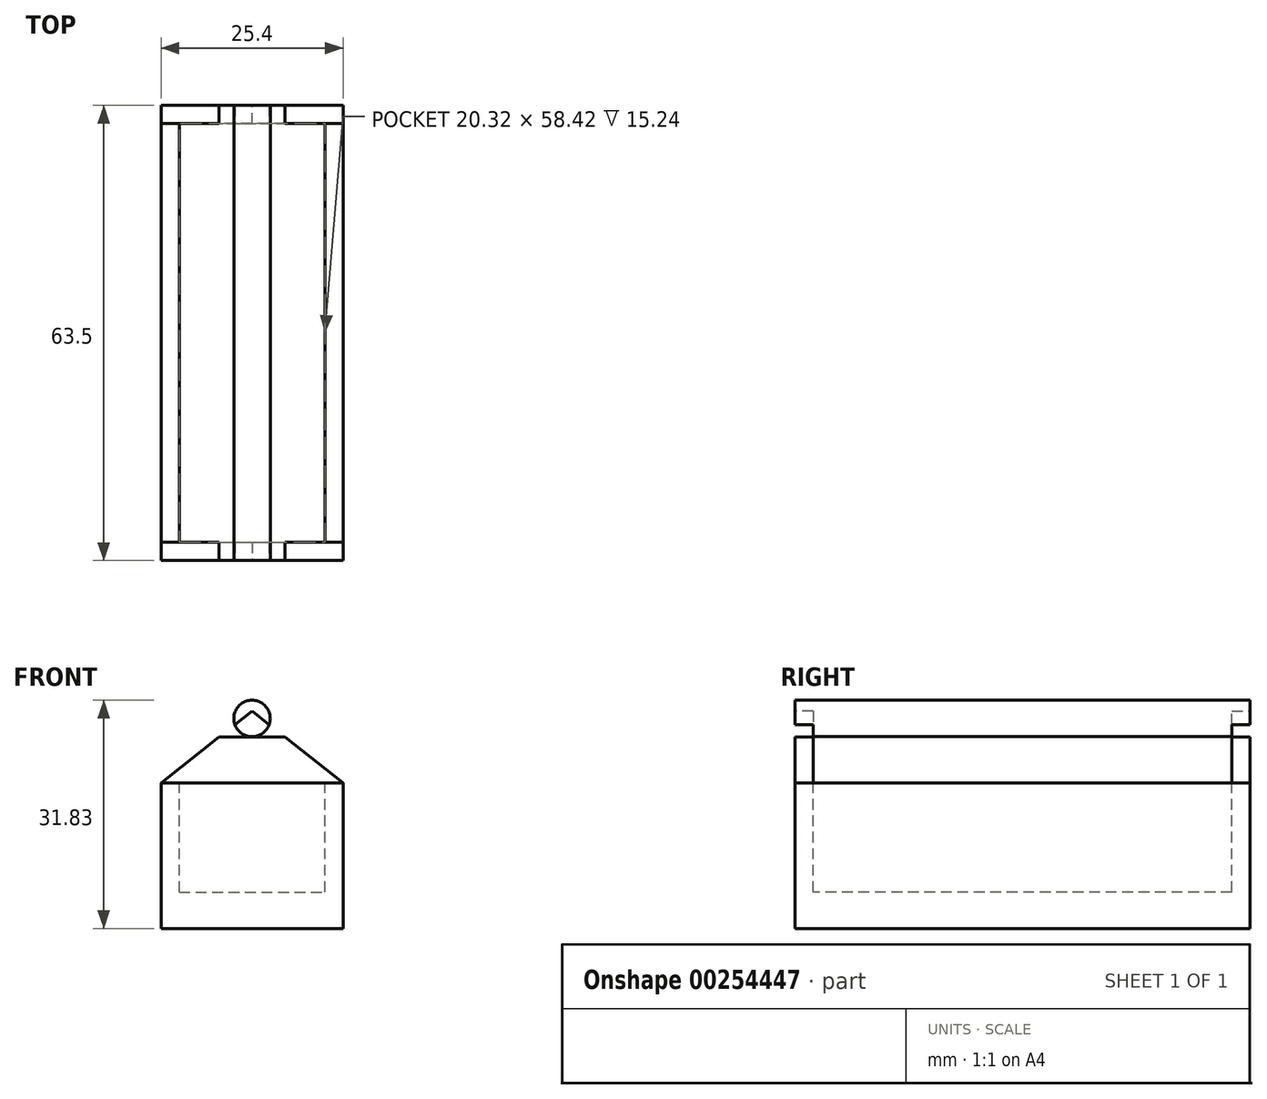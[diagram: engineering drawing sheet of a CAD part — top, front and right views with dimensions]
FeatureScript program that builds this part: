
annotation { "Feature Type Name" : "Feature", "Feature Type Description" : "" }
export const myFeature = defineFeature(function(context is Context, id is Id, definition is map)
    precondition{}
    {
        {
            var Q0;
            Q0=qCreatedBy(makeId("Top.planeOp"),FACE);
            var sketch = newSketch(context, id + "F0", { "sketchPlane" : qUnion([Q0])});
            skLineSegment(sketch, "E0.bottom", {"start": v(-12.7, 31.75) * mm, "end": v(12.7, 31.75) * mm});
            skLineSegment(sketch, "E0.top", {"start": v(-12.7, -31.75) * mm, "end": v(12.7, -31.75) * mm});
            skLineSegment(sketch, "E0.left", {"start": v(-12.7, 31.75) * mm, "end": v(-12.7, -31.75) * mm});
            skLineSegment(sketch, "E0.right", {"start": v(12.7, 31.75) * mm, "end": v(12.7, -31.75) * mm});
            skPoint(sketch, "E0.middle", {"position": v(0, 0) * mm});
            skSolve(sketch);
        }
        {
            var Q0;
            Q0=makeQuery(id+"F0.imprint","IMPRINT",FACE,{"disambiguationData":[TD([[makeQuery(id+"F0.imprint","IMPRINT",EDGE,{"derivedFrom":sQuery(id+"F0.wireOp",EDGE,"E0.bottom")}),-1.0]])]});
            extrude(context, id + "F1", {"entities" : qUnion([Q0]), "depth" : 20.32 * mm});
        }
        {
            var Q0;
            Q0=makeQuery(id+"F1.opExtrude","CAP_FACE",FACE,{"disambiguationData":[OSD([sQuery(id+"F0.wireOp",EDGE,"E0.bottom"),sQuery(id+"F0.wireOp",EDGE,"E0.top"),sQuery(id+"F0.wireOp",EDGE,"E0.left"),sQuery(id+"F0.wireOp",EDGE,"E0.right")])],"isStart":false});
            var sketch = newSketch(context, id + "F2", { "sketchPlane" : qUnion([Q0])});
            skLineSegment(sketch, "E1.bottom", {"start": v(-10.16, 29.2) * mm, "end": v(10.16, 29.2) * mm});
            skLineSegment(sketch, "E1.top", {"start": v(-10.16, -29.21) * mm, "end": v(10.16, -29.21) * mm});
            skLineSegment(sketch, "E1.left", {"start": v(-10.16, 29.2) * mm, "end": v(-10.16, -29.21) * mm});
            skLineSegment(sketch, "E1.right", {"start": v(10.16, 29.2) * mm, "end": v(10.16, -29.21) * mm});
            skPoint(sketch, "E1.middle", {"position": v(0, 0) * mm});
            skSolve(sketch);
        }
        {
            var Q0;
            Q0 = qSketchRegion(id + "F2", true);
            extrude(context, id + "F3", {"entities" : qUnion([Q0]), "operationType" : NewBodyOperationType.REMOVE, "oppositeDirection" : true, "depth" : 15.24 * mm});
        }
        {
            var Q0;
            Q0=qCreatedBy(makeId("Right.planeOp"),FACE);
            var sketch = newSketch(context, id + "F4", { "sketchPlane" : qUnion([Q0])});
            skLineSegment(sketch, "E2.bottom", {"start": v(-31.75, 29.29) * mm, "end": v(31.75, 29.29) * mm});
            skLineSegment(sketch, "E2.top", {"start": v(-31.75, 31.83) * mm, "end": v(31.75, 31.83) * mm});
            skLineSegment(sketch, "E2.left", {"start": v(-31.75, 29.29) * mm, "end": v(-31.75, 31.83) * mm});
            skLineSegment(sketch, "E2.right", {"start": v(31.75, 29.29) * mm, "end": v(31.75, 31.83) * mm});
            skSolve(sketch);
        }
        {
            var Q0;
            Q0 = qSketchRegion(id + "F4", true);
            var Q1;
            Q1=sQuery(id+"F4.wireOp",EDGE,"E2.bottom");
            revolve(context, id + "F5", {"entities" : qUnion([Q0]), "axis" : qUnion([Q1]), "revolveType" : RevolveType.FULL});
        }
        {
            var Q0;
            Q0=makeQuery(id+"F1.opExtrude","SWEPT_FACE",FACE,{"disambiguationData":[OSD([sQuery(id+"F0.wireOp",EDGE,"E0.top")])]});
            var sketch = newSketch(context, id + "F6", { "sketchPlane" : qUnion([Q0])});
            skLineSegment(sketch, "E3", {"start": v(-12.7, 20.32) * mm, "end": v(0, 30.32) * mm});
            skLineSegment(sketch, "E4", {"start": v(0, 30.32) * mm, "end": v(12.7, 20.32) * mm});
            skLineSegment(sketch, "E5", {"start": v(12.7, 20.32) * mm, "end": v(-12.7, 20.32) * mm});
            skSolve(sketch);
        }
        {
            var Q0;
            Q0=makeQuery(id+"F6.imprint","IMPRINT",FACE,{"disambiguationData":[TD([[makeQuery(id+"F6.imprint","IMPRINT",EDGE,{"derivedFrom":sQuery(id+"F6.wireOp",EDGE,"E3")}),-1.0]])]});
            extrude(context, id + "F7", {"entities" : qUnion([Q0]), "oppositeDirection" : true, "depth" : 2.54 * mm});
        }
        {
            var Q0;
            Q0=makeQuery(id+"F1.opExtrude","SWEPT_FACE",FACE,{"disambiguationData":[OSD([sQuery(id+"F0.wireOp",EDGE,"E0.bottom")])]});
            var sketch = newSketch(context, id + "F8", { "sketchPlane" : qUnion([Q0])});
            skLineSegment(sketch, "E6", {"start": v(-12.7, 20.32) * mm, "end": v(12.7, 20.32) * mm});
            skLineSegment(sketch, "E7", {"start": v(12.7, 20.32) * mm, "end": v(0, 30.32) * mm});
            skLineSegment(sketch, "E8", {"start": v(-12.7, 20.32) * mm, "end": v(0, 30.32) * mm});
            skSolve(sketch);
        }
        {
            var Q0;
            Q0 = qSketchRegion(id + "F8", true);
            extrude(context, id + "F9", {"entities" : qUnion([Q0]), "oppositeDirection" : true, "depth" : 2.54 * mm});
        }
        {
            var Q0;
            Q0=makeQuery(id+"F7.opExtrude","CAP_FACE",FACE,{"disambiguationData":[OSD([sQuery(id+"F6.wireOp",EDGE,"E3"),sQuery(id+"F6.wireOp",EDGE,"E4"),sQuery(id+"F6.wireOp",EDGE,"E5")])],"isStart":true});
            var sketch = newSketch(context, id + "F10", { "sketchPlane" : qUnion([Q0])});
            skLineSegment(sketch, "E9", {"start": v(0, 26.7) * mm, "end": v(4.61, 26.7) * mm});
            skLineSegment(sketch, "E10", {"start": v(4.61, 26.7) * mm, "end": v(0, 30.32) * mm});
            skLineSegment(sketch, "E11", {"start": v(0, 30.32) * mm, "end": v(-4.61, 26.7) * mm});
            skLineSegment(sketch, "E12", {"start": v(-4.61, 26.7) * mm, "end": v(0, 26.7) * mm});
            skSolve(sketch);
        }
        {
            var Q0;
            Q0 = qSketchRegion(id + "F10", true);
            extrude(context, id + "F11", {"entities" : qUnion([Q0]), "operationType" : NewBodyOperationType.REMOVE, "oppositeDirection" : true, "depth" : 2.54 * mm});
        }
        {
            var Q0;
            Q0=makeQuery(id+"F9.opExtrude","CAP_FACE",FACE,{"disambiguationData":[OSD([sQuery(id+"F8.wireOp",EDGE,"E6"),sQuery(id+"F8.wireOp",EDGE,"E7"),sQuery(id+"F8.wireOp",EDGE,"E8")])],"isStart":true});
            var sketch = newSketch(context, id + "F12", { "sketchPlane" : qUnion([Q0])});
            skLineSegment(sketch, "E13", {"start": v(0, 26.71) * mm, "end": v(4.58, 26.71) * mm});
            skLineSegment(sketch, "E14", {"start": v(0, 30.32) * mm, "end": v(4.58, 26.71) * mm});
            skLineSegment(sketch, "E15", {"start": v(0, 30.32) * mm, "end": v(-4.58, 26.71) * mm});
            skLineSegment(sketch, "E16", {"start": v(-4.58, 26.71) * mm, "end": v(0, 26.71) * mm});
            skSolve(sketch);
        }
        {
            var Q0;
            Q0 = qSketchRegion(id + "F12", true);
            extrude(context, id + "F13", {"entities" : qUnion([Q0]), "operationType" : NewBodyOperationType.REMOVE, "oppositeDirection" : true, "depth" : 2.54 * mm});
        }
    });
